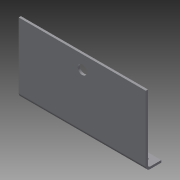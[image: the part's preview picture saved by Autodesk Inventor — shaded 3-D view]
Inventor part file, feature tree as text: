
AUTODESK INVENTOR PART (.ipt)
format: ipt  version: 2014 (Build 180170000, 170)  size: 102,912 bytes
history: native  units: in
note: dims shown in document units (in); Inventor stores cm internally (conversion verified against a paired STEP export)
features: sheet_metal_op x2, sketch x1, other x1
ambient origin geometry x8: Origin, YZ Plane, XZ Plane, XY Plane, X Axis, Y Axis, Z Axis, Center Point
bodies: Solid1 (feature_tree)
feature tree (4):
  sketch  "Sketch1"  dims[d0=7.0in d1=4.5in d2=0.375in d3=0.5in d4=0.375in d5=0.5in d7=0.25in d8=0.25in d9=0.5in d10=0.75in d11=3.0in d12=0.12in d13=0.12in d14=0.06in d15=0.24in d16=0.12in d17=90.0deg d18=0.12in]
  sheet_metal_op  "Face1"
  sheet_metal_op  "Fold1"
  other  "Plate1"
